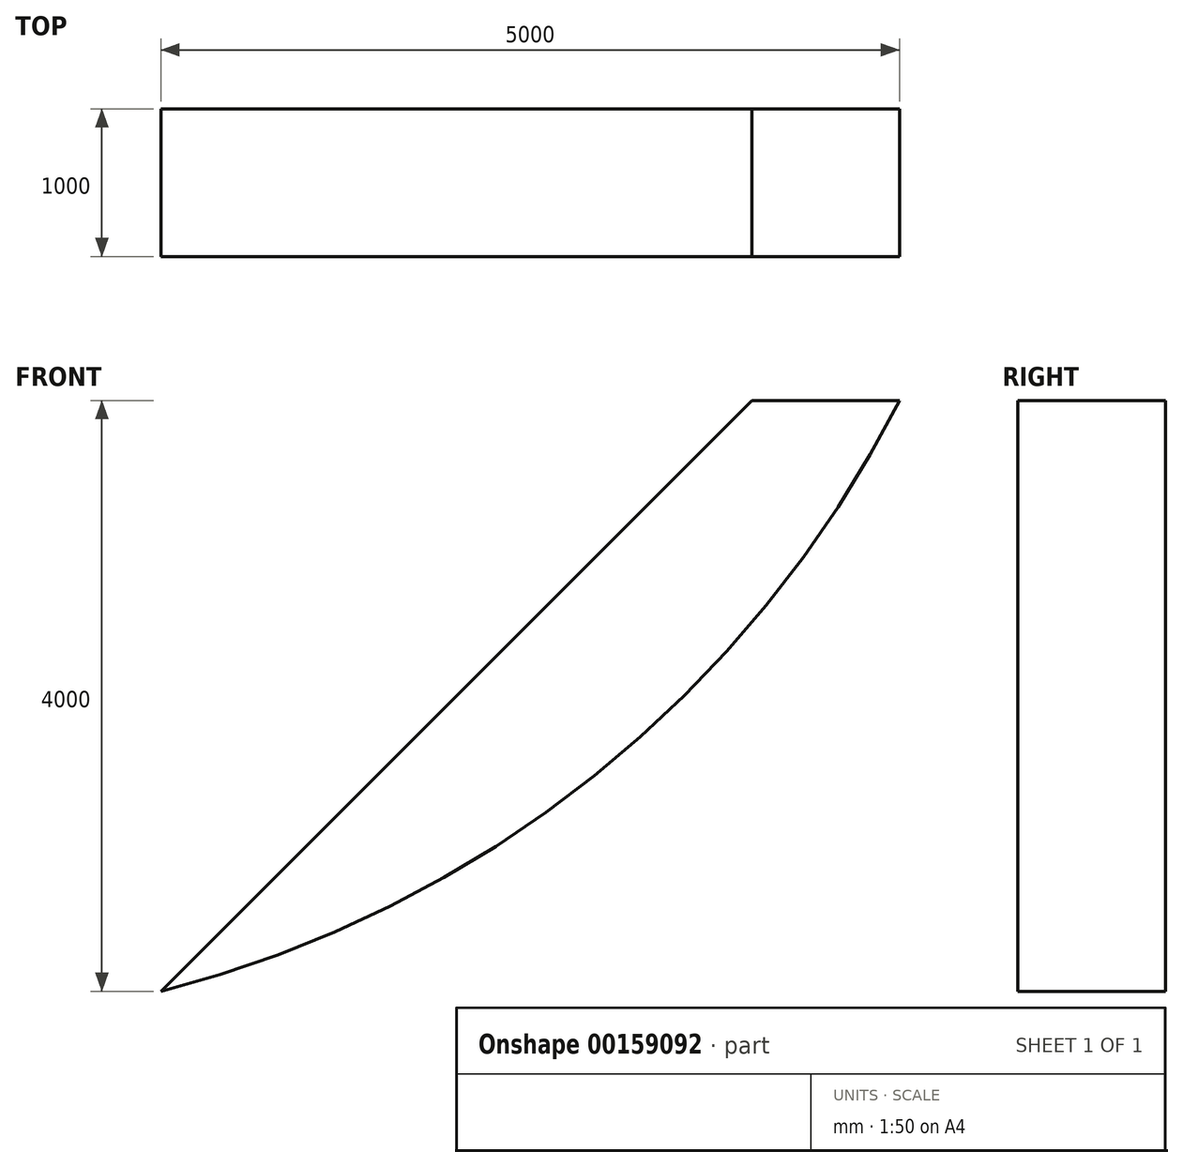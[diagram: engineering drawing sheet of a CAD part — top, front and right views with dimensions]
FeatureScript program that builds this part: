
annotation { "Feature Type Name" : "Feature", "Feature Type Description" : "" }
export const myFeature = defineFeature(function(context is Context, id is Id, definition is map)
    precondition{}
    {
        {
            var Q0;
            Q0=qCreatedBy(makeId("Front.planeOp"),FACE);
            var sketch = newSketch(context, id + "F0", { "sketchPlane" : qUnion([Q0])});
            skArc(sketch, "E0", {"start": v(-2765.3, -1572.83) * mm, "mid": v(168.3, -114.81) * mm, "end": v(2234.7, 2427.17) * mm});
            skLineSegment(sketch, "E1", {"start": v(2234.7, 2427.17) * mm, "end": v(1234.7, 2427.17) * mm});
            skLineSegment(sketch, "E2", {"start": v(1234.7, 2427.17) * mm, "end": v(-2765.3, -1572.83) * mm});
            skSolve(sketch);
        }
        {
            var Q0;
            Q0=makeQuery(id+"F0.imprint","IMPRINT",FACE,{"disambiguationData":[TD([[makeQuery(id+"F0.imprint","IMPRINT",EDGE,{"derivedFrom":sQuery(id+"F0.wireOp",EDGE,"E0")}),1.0]])]});
            extrude(context, id + "F1", {"entities" : qUnion([Q0]), "depth" : 1000 * mm});
        }
    });
